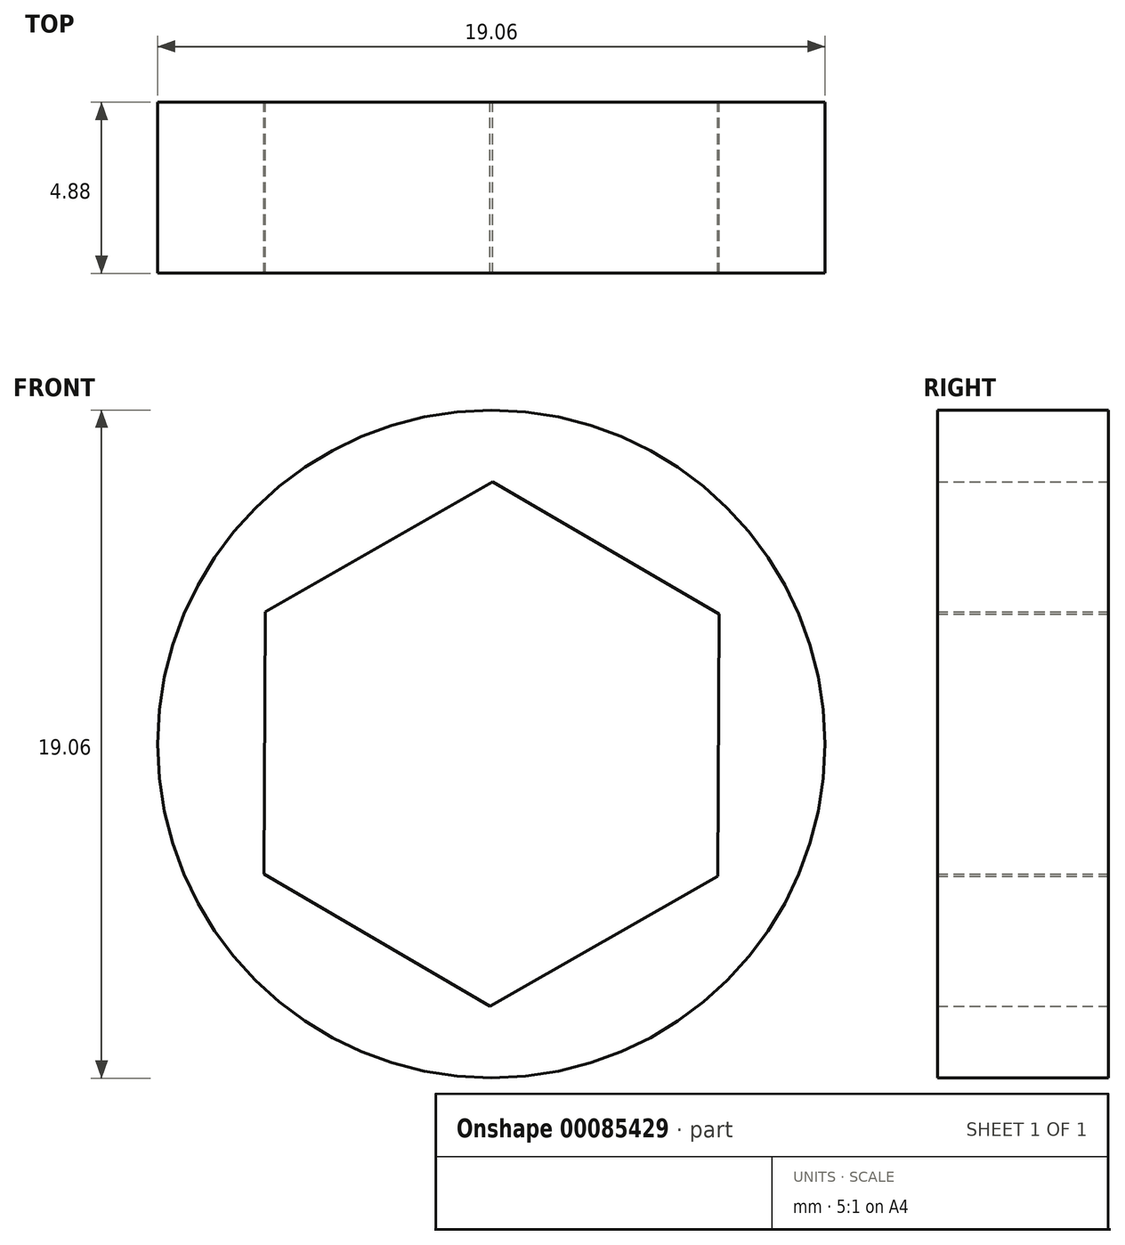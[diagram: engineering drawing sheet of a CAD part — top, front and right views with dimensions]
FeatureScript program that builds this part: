
annotation { "Feature Type Name" : "Feature", "Feature Type Description" : "" }
export const myFeature = defineFeature(function(context is Context, id is Id, definition is map)
    precondition{}
    {
        {
            var Q0;
            Q0=qCreatedBy(makeId("Front.planeOp"),FACE);
            var sketch = newSketch(context, id + "F0", { "sketchPlane" : qUnion([Q0])});
            skCircle(sketch, "E0", {"center": v(0, 0) * mm, "radius": 9.53 * mm});
            skCircle(sketch, "E1.cCircle", {"center": v(0, 0) * mm, "radius": 6.48 * mm, "construction": true});
            skLineSegment(sketch, "E1.0", {"start": v(0.04, 7.48) * mm, "end": v(6.5, 3.7) * mm});
            skLineSegment(sketch, "E1.1", {"start": v(6.5, 3.7) * mm, "end": v(6.46, -3.77) * mm});
            skLineSegment(sketch, "E1.2", {"start": v(6.46, -3.77) * mm, "end": v(-0.04, -7.48) * mm});
            skLineSegment(sketch, "E1.3", {"start": v(-0.04, -7.48) * mm, "end": v(-6.5, -3.7) * mm});
            skLineSegment(sketch, "E1.4", {"start": v(-6.5, -3.7) * mm, "end": v(-6.46, 3.77) * mm});
            skLineSegment(sketch, "E1.5", {"start": v(-6.46, 3.77) * mm, "end": v(0.04, 7.48) * mm});
            skPoint(sketch, "E1.0.midPoint", {"position": v(3.27, 5.6) * mm});
            skSolve(sketch);
        }
        {
            var Q0;
            Q0=makeQuery(id+"F0.imprint","IMPRINT",FACE,{"disambiguationData":[TD([[makeQuery(id+"F0.imprint","IMPRINT",EDGE,{"derivedFrom":sQuery(id+"F0.wireOp",EDGE,"E0")}),1.0]])]});
            extrude(context, id + "F1", {"entities" : qUnion([Q0]), "depth" : 4.88 * mm});
        }
    });
